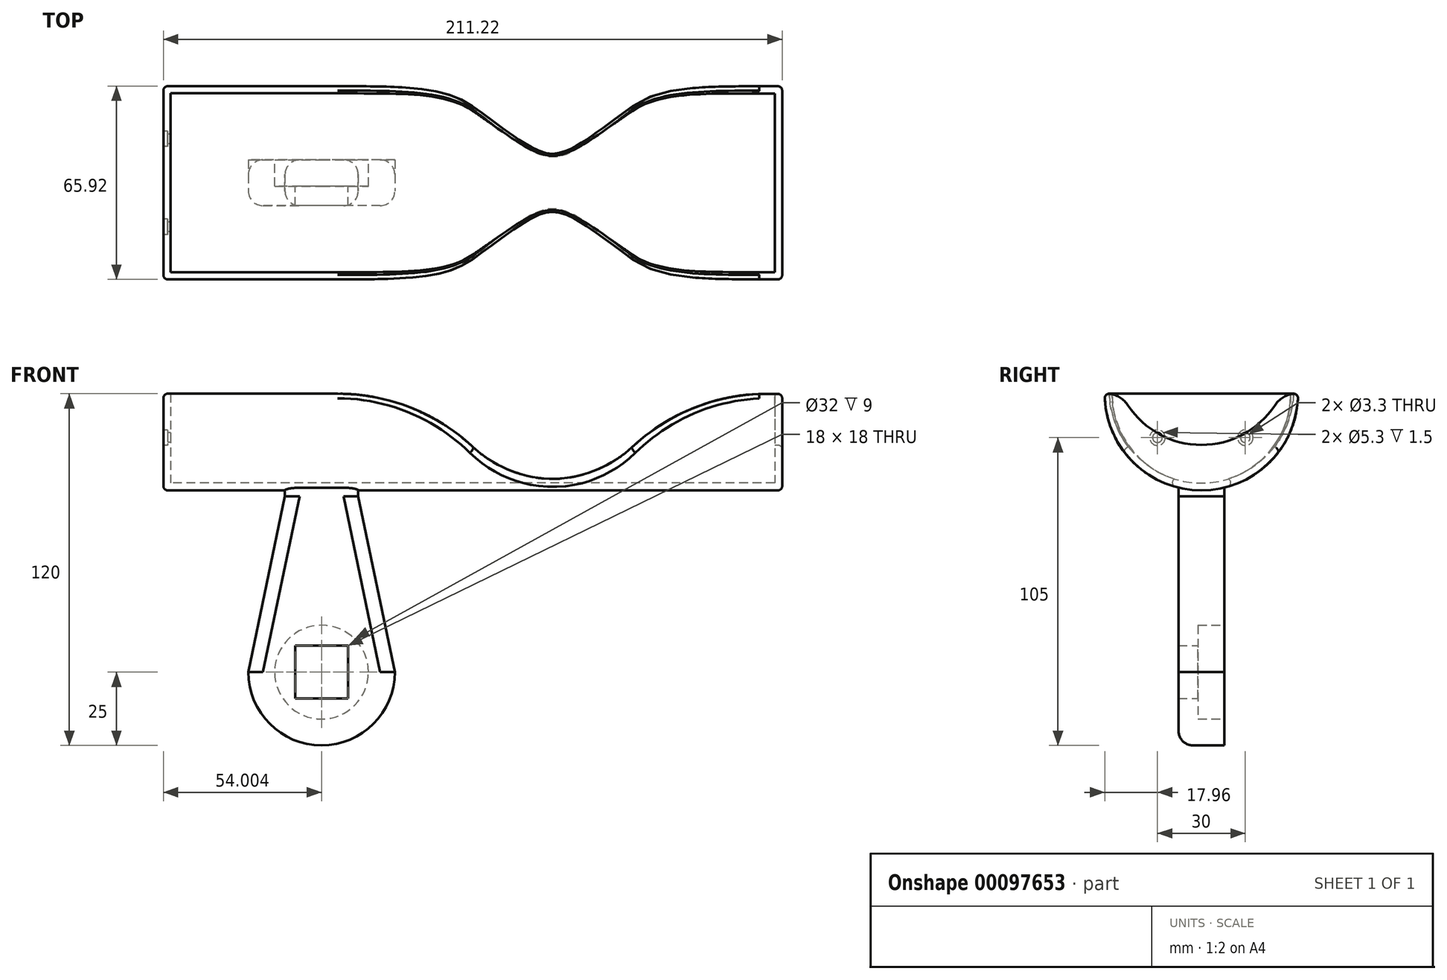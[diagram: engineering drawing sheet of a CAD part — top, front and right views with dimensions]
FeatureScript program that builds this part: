
annotation { "Feature Type Name" : "Feature", "Feature Type Description" : "" }
export const myFeature = defineFeature(function(context is Context, id is Id, definition is map)
    precondition{}
    {
        {
            var Q0;
            Q0=qCreatedBy(makeId("Right.planeOp"),FACE);
            var sketch = newSketch(context, id + "F0", { "sketchPlane" : qUnion([Q0])});
            skArc(sketch, "E0", {"start": v(-33, 0) * mm, "mid": v(0, -33) * mm, "end": v(33, 0) * mm});
            skLineSegment(sketch, "E1", {"start": v(-33, 0) * mm, "end": v(33, 0) * mm});
            skSolve(sketch);
        }
        {
            var Q0;
            Q0=makeQuery(id+"F0.imprint","IMPRINT",FACE,{"disambiguationData":[TD([[makeQuery(id+"F0.imprint","IMPRINT",EDGE,{"derivedFrom":sQuery(id+"F0.wireOp",EDGE,"E0")}),1.0]])]});
            extrude(context, id + "F1", {"entities" : qUnion([Q0]), "endBound" : BoundingType.SYMMETRIC, "depth" : 211.21 * mm});
        }
        {
            var Q0;
            Q0=makeQuery(id+"F1.opExtrude","SWEPT_FACE",FACE,{"disambiguationData":[OSD([sQuery(id+"F0.wireOp",EDGE,"E1")])]});
            shell(context, id + "F2", {"entities" : qUnion([Q0]), "thickness" : 2.5 * mm});
        }
        {
            var Q0;
            Q0=qCreatedBy(makeId("Front.planeOp"),FACE);
            var sketch = newSketch(context, id + "F3", { "sketchPlane" : qUnion([Q0])});
            skArc(sketch, "E2", {"start": v(0, -18.13) * mm, "mid": v(-21.33, -4.7) * mm, "end": v(-46.1, 0) * mm});
            skArc(sketch, "E3", {"start": v(0, -18.13) * mm, "mid": v(27.25, -28.85) * mm, "end": v(54.5, -18.13) * mm});
            skArc(sketch, "E4", {"start": v(100.6, 0) * mm, "mid": v(75.83, -4.7) * mm, "end": v(54.5, -18.13) * mm});
            skLineSegment(sketch, "E5", {"start": v(-46.1, 0) * mm, "end": v(100.6, 0) * mm});
            skSolve(sketch);
        }
        {
            var Q0;
            Q0 = qSketchRegion(id + "F3", true);
            extrude(context, id + "F4", {"entities" : qUnion([Q0]), "operationType" : NewBodyOperationType.REMOVE, "endBound" : BoundingType.SYMMETRIC, "oppositeDirection" : true, "depth" : 70 * mm});
        }
        {
            var Q0;
            Q0=makeQuery(id+"F1.opExtrude","CAP_FACE",FACE,{"disambiguationData":[OSD([sQuery(id+"F0.wireOp",EDGE,"E0"),sQuery(id+"F0.wireOp",EDGE,"E1")])],"isStart":false});
            var sketch = newSketch(context, id + "F5", { "sketchPlane" : qUnion([Q0])});
            skArc(sketch, "E6", {"start": v(-25.04, -4) * mm, "mid": v(-28.49, -0.94) * mm, "end": v(-33, 0) * mm});
            skArc(sketch, "E7", {"start": v(-25.04, -4) * mm, "mid": v(0, -17.48) * mm, "end": v(25.04, -4) * mm});
            skArc(sketch, "E8", {"start": v(33, 0) * mm, "mid": v(28.49, -0.94) * mm, "end": v(25.04, -4) * mm});
            skLineSegment(sketch, "E9", {"start": v(-33, 0) * mm, "end": v(33, 0) * mm});
            skSolve(sketch);
        }
        {
            var Q0;
            Q0=makeQuery(id+"F5.imprint","IMPRINT",FACE,{"disambiguationData":[TD([[makeQuery(id+"F5.imprint","IMPRINT",EDGE,{"derivedFrom":sQuery(id+"F5.wireOp",EDGE,"E6")}),-1.0]])]});
            extrude(context, id + "F6", {"entities" : qUnion([Q0]), "operationType" : NewBodyOperationType.REMOVE, "endBound" : BoundingType.UP_TO_NEXT, "oppositeDirection" : true, "depth" : 25 * mm});
        }
        {
            var Q0;
            Q0=makeQuery(id+"F4.boolean.opBoolean","INTERSECT",EDGE,{"disambiguationData":[OD(0.0)],"derivedFrom":[makeQuery(id+"F1.opExtrude","SWEPT_FACE",FACE,{"disambiguationData":[OSD([sQuery(id+"F0.wireOp",EDGE,"E0")])]}),makeQuery(id+"F4.opExtrude","SWEPT_FACE",FACE,{"disambiguationData":[OSD([sQuery(id+"F3.wireOp",EDGE,"E2")])]})]});
            fillet(context, id + "F7", {"entities" : qUnion([Q0]), "radius" : 1.5 * mm, "tangentPropagation" : true, "allowEdgeOverflow" : false});
        }
        {
            var Q0;
            Q0=makeQuery(id+"F4.boolean.opBoolean","INTERSECT",EDGE,{"disambiguationData":[OD(1.0)],"derivedFrom":[makeQuery(id+"F1.opExtrude","SWEPT_FACE",FACE,{"disambiguationData":[OSD([sQuery(id+"F0.wireOp",EDGE,"E0")])]}),makeQuery(id+"F4.opExtrude","SWEPT_FACE",FACE,{"disambiguationData":[OSD([sQuery(id+"F3.wireOp",EDGE,"E3")])]})]});
            fillet(context, id + "F8", {"entities" : qUnion([Q0]), "radius" : 1.5 * mm, "tangentPropagation" : true, "allowEdgeOverflow" : false});
        }
        {
            var Q0;
            Q0=makeQuery(id+"F1.opExtrude","CAP_FACE",FACE,{"disambiguationData":[OSD([sQuery(id+"F0.wireOp",EDGE,"E0"),sQuery(id+"F0.wireOp",EDGE,"E1")])],"isStart":false});
            var Q1;
            Q1=makeQuery(id+"F1.opExtrude","CAP_FACE",FACE,{"disambiguationData":[OSD([sQuery(id+"F0.wireOp",EDGE,"E0"),sQuery(id+"F0.wireOp",EDGE,"E1")])],"isStart":true});
            fillet(context, id + "F9", {"entities" : qUnion([Q0, Q1]), "radius" : 1.5 * mm, "tangentPropagation" : true, "allowEdgeOverflow" : false});
        }
        {
            var Q0;
            Q0=makeQuery(id+"F1.opExtrude","CAP_FACE",FACE,{"disambiguationData":[OSD([sQuery(id+"F0.wireOp",EDGE,"E0"),sQuery(id+"F0.wireOp",EDGE,"E1")])],"isStart":true});
            var sketch = newSketch(context, id + "F10", { "sketchPlane" : qUnion([Q0])});
            skPoint(sketch, "E10", {"position": v(15, -15) * mm});
            skPoint(sketch, "E11.MirrorP", {"position": v(-15, -15) * mm});
            skSolve(sketch);
        }
        {
            var Q0;
            Q0=sQuery(id+"F10.wireOp",VERTEX,"E10");
            var Q1;
            Q1=sQuery(id+"F10.wireOp",VERTEX,"E11.MirrorP");
            var Q2;
            Q2=makeQuery(id+"F1.opExtrude","SWEPT_BODY",BODY,{"disambiguationData":[OSD([sQuery(id+"F0.wireOp",EDGE,"E0"),sQuery(id+"F0.wireOp",EDGE,"E1")])]});
            hole(context, id + "F11", {"style" : HoleStyle.SIMPLE, "endStyle" : HoleEndStyle.BLIND, "standardTappedOrClearance" : lookupTablePath({ "standard" : "ISO", "fit" : "Normal", "size" : "M3", "type" : "Clearance" }), "standardBlindInLast" : lookupTablePath({ "fit" : "Standard", "standard" : "ISO", "size" : "M3", "type" : "Clearance" }), "holeDiameter" : 3.3 * mm, "holeDepth" : 2.5 * mm, "locations" : qUnion([Q0, Q1]), "scope" : qUnion([Q2])});
        }
        {
            var Q0;
            Q0=makeQuery(id+"F1.opExtrude","CAP_FACE",FACE,{"disambiguationData":[OSD([sQuery(id+"F0.wireOp",EDGE,"E0"),sQuery(id+"F0.wireOp",EDGE,"E1")])],"isStart":true});
            var sketch = newSketch(context, id + "F12", { "sketchPlane" : qUnion([Q0])});
            skCircle(sketch, "E12", {"center": v(15, -15) * mm, "radius": 2.65 * mm});
            skCircle(sketch, "E13.MirrorC", {"center": v(-15, -15) * mm, "radius": 2.65 * mm});
            skSolve(sketch);
        }
        {
            var Q0;
            Q0 = qSketchRegion(id + "F12", true);
            extrude(context, id + "F13", {"entities" : qUnion([Q0]), "operationType" : NewBodyOperationType.REMOVE, "oppositeDirection" : true, "depth" : 1.5 * mm});
        }
        {
            var Q0;
            Q0=qCreatedBy(makeId("Top.planeOp"),FACE);
            cPlane(context, id + "F14", {"entities" : qUnion([Q0]), "cplaneType" : CPlaneType.OFFSET, "offset" : 35 * mm, "oppositeDirection" : true, "width" : 150 * mm, "height" : 150 * mm});
        }
        {
            var Q0;
            Q0=qCreatedBy(id+"F14.planeOp",FACE);
            var sketch = newSketch(context, id + "F15", { "sketchPlane" : qUnion([Q0])});
            skLineSegment(sketch, "E14.bottom", {"start": v(-59.1, -7.83) * mm, "end": v(-44.1, -7.83) * mm});
            skLineSegment(sketch, "E14.top", {"start": v(-59.1, 7.83) * mm, "end": v(-44.1, 7.83) * mm});
            skLineSegment(sketch, "E14.left", {"start": v(-64.1, -2.82) * mm, "end": v(-64.1, 2.82) * mm});
            skLineSegment(sketch, "E14.right", {"start": v(-39.1, -2.83) * mm, "end": v(-39.1, 2.83) * mm});
            skPoint(sketch, "E15.visualSharp", {"position": v(-64.1, -7.82) * mm});
            skArc(sketch, "E15.filletArc", {"start": v(-64.1, -2.82) * mm, "mid": v(-62.64, -6.36) * mm, "end": v(-59.1, -7.82) * mm});
            skPoint(sketch, "E16.visualSharp", {"position": v(-64.1, 7.82) * mm});
            skArc(sketch, "E16.filletArc", {"start": v(-59.1, 7.82) * mm, "mid": v(-62.64, 6.36) * mm, "end": v(-64.1, 2.82) * mm});
            skPoint(sketch, "E17.visualSharp", {"position": v(-39.1, -7.83) * mm});
            skArc(sketch, "E17.filletArc", {"start": v(-44.1, -7.83) * mm, "mid": v(-40.57, -6.36) * mm, "end": v(-39.1, -2.83) * mm});
            skPoint(sketch, "E18.visualSharp", {"position": v(-39.1, 7.83) * mm});
            skArc(sketch, "E18.filletArc", {"start": v(-39.1, 2.83) * mm, "mid": v(-40.57, 6.36) * mm, "end": v(-44.1, 7.83) * mm});
            skSolve(sketch);
        }
        {
            var Q0;
            Q0=qCreatedBy(id+"F14.planeOp",FACE);
            cPlane(context, id + "F16", {"entities" : qUnion([Q0]), "cplaneType" : CPlaneType.OFFSET, "offset" : 60 * mm, "oppositeDirection" : true, "width" : 150 * mm, "height" : 150 * mm});
        }
        {
            var Q0;
            Q0=qCreatedBy(id+"F16.planeOp",FACE);
            var sketch = newSketch(context, id + "F17", { "sketchPlane" : qUnion([Q0])});
            skLineSegment(sketch, "E19.bottom", {"start": v(-71.6, 7.83) * mm, "end": v(-31.6, 7.83) * mm});
            skLineSegment(sketch, "E19.top", {"start": v(-71.6, -7.83) * mm, "end": v(-31.6, -7.83) * mm});
            skLineSegment(sketch, "E19.left", {"start": v(-76.6, 2.82) * mm, "end": v(-76.6, -2.83) * mm});
            skLineSegment(sketch, "E19.right", {"start": v(-26.6, 2.83) * mm, "end": v(-26.6, -2.82) * mm});
            skPoint(sketch, "E20.visualSharp", {"position": v(-76.6, 7.83) * mm});
            skArc(sketch, "E20.filletArc", {"start": v(-71.6, 7.83) * mm, "mid": v(-75.14, 6.36) * mm, "end": v(-76.6, 2.82) * mm});
            skPoint(sketch, "E21.visualSharp", {"position": v(-26.6, 7.83) * mm});
            skArc(sketch, "E21.filletArc", {"start": v(-26.6, 2.83) * mm, "mid": v(-28.07, 6.36) * mm, "end": v(-31.6, 7.83) * mm});
            skPoint(sketch, "E22.visualSharp", {"position": v(-26.6, -7.83) * mm});
            skArc(sketch, "E22.filletArc", {"start": v(-31.6, -7.83) * mm, "mid": v(-28.07, -6.36) * mm, "end": v(-26.6, -2.82) * mm});
            skPoint(sketch, "E23.visualSharp", {"position": v(-76.6, -7.83) * mm});
            skArc(sketch, "E23.filletArc", {"start": v(-76.6, -2.83) * mm, "mid": v(-75.14, -6.36) * mm, "end": v(-71.6, -7.83) * mm});
            skSolve(sketch);
        }
        {
            var Q0;
            Q0=makeQuery(id+"F15.imprint","IMPRINT",FACE,{"disambiguationData":[TD([[makeQuery(id+"F15.imprint","IMPRINT",EDGE,{"derivedFrom":sQuery(id+"F15.wireOp",EDGE,"E14.bottom")}),1.0]])]});
            var Q1;
            Q1=makeQuery(id+"F1.opExtrude","SWEPT_FACE",FACE,{"disambiguationData":[OSD([sQuery(id+"F0.wireOp",EDGE,"E0")])]});
            var Q2;
            Q2=makeQuery(id+"F1.opExtrude","SWEPT_BODY",BODY,{"disambiguationData":[OSD([sQuery(id+"F0.wireOp",EDGE,"E0"),sQuery(id+"F0.wireOp",EDGE,"E1")])]});
            extrude(context, id + "F18", {"entities" : qUnion([Q0]), "operationType" : NewBodyOperationType.ADD, "endBound" : BoundingType.UP_TO_NEXT, "endBoundEntityFace" : qUnion([Q1]), "endBoundEntityBody" : qUnion([Q2]), "depth" : 25 * mm});
        }
        {
            var Q1;
            Q1=makeQuery(id+"F17.imprint","IMPRINT",FACE,{"disambiguationData":[TD([[makeQuery(id+"F17.imprint","IMPRINT",EDGE,{"derivedFrom":sQuery(id+"F17.wireOp",EDGE,"E19.bottom")}),-1.0]])]});
            var Q2;
            Q2=makeQuery(id+"F15.imprint","IMPRINT",FACE,{"disambiguationData":[TD([[makeQuery(id+"F15.imprint","IMPRINT",EDGE,{"derivedFrom":sQuery(id+"F15.wireOp",EDGE,"E14.bottom")}),1.0]])]});
            loft(context, id + "F19", {"operationType" : NewBodyOperationType.ADD, "sheetProfilesArray" : [{ "sheetProfileEntities" : qUnion([Q1]) }, { "sheetProfileEntities" : qUnion([Q2]) }]});
        }
        {
            var Q0;
            Q0=makeQuery(id+"F19.opLoft","SWEPT_FACE",FACE,{"disambiguationData":[OSD([sQuery(id+"F15.wireOp",EDGE,"E14.bottom"),sQuery(id+"F15.wireOp",EDGE,"E15.filletArc"),sQuery(id+"F15.wireOp",EDGE,"E17.filletArc"),sQuery(id+"F17.wireOp",EDGE,"E19.top"),sQuery(id+"F17.wireOp",EDGE,"E22.filletArc"),sQuery(id+"F17.wireOp",EDGE,"E23.filletArc")])]});
            var sketch = newSketch(context, id + "F20", { "sketchPlane" : qUnion([Q0])});
            skArc(sketch, "E24", {"start": v(-76.6, -95) * mm, "mid": v(-51.6, -120) * mm, "end": v(-26.6, -95) * mm});
            skLineSegment(sketch, "E25", {"start": v(-26.6, -95) * mm, "end": v(-76.6, -95) * mm});
            skSolve(sketch);
        }
        {
            var Q0;
            {var subQ0=sQuery(id+"F20.wireOp",EDGE,"E24");Q0=makeQuery(id+"F20.imprint","IMPRINT",FACE,{"disambiguationData":[TD([[makeQuery(id+"F20.imprint","IMPRINT",EDGE,{"derivedFrom":subQ0}),1.0]])]});}
            var Q1;
            Q1=makeQuery(id+"F19.opLoft","SWEPT_FACE",FACE,{"disambiguationData":[OSD([sQuery(id+"F15.wireOp",EDGE,"E14.top"),sQuery(id+"F15.wireOp",EDGE,"E16.filletArc"),sQuery(id+"F15.wireOp",EDGE,"E18.filletArc"),sQuery(id+"F17.wireOp",EDGE,"E19.bottom"),sQuery(id+"F17.wireOp",EDGE,"E20.filletArc"),sQuery(id+"F17.wireOp",EDGE,"E21.filletArc")])]});
            extrude(context, id + "F21", {"entities" : qUnion([Q0]), "operationType" : NewBodyOperationType.ADD, "endBound" : BoundingType.UP_TO_SURFACE, "oppositeDirection" : true, "endBoundEntityFace" : qUnion([Q1]), "depth" : 25 * mm});
        }
        {
            var Q0;
            Q0=makeQuery(id+"F21.opExtrude","CAP_EDGE",EDGE,{"disambiguationData":[OSD([sQuery(id+"F20.wireOp",EDGE,"E24")])],"isStart":true});
            var Q1;
            Q1=makeQuery(id+"F21.opExtrude","TWEAK_EDGE",EDGE,{"derivedFrom":[makeQuery(id+"F19.opLoft","SWEPT_FACE",FACE,{"disambiguationData":[OSD([sQuery(id+"F15.wireOp",EDGE,"E14.top"),sQuery(id+"F15.wireOp",EDGE,"E16.filletArc"),sQuery(id+"F15.wireOp",EDGE,"E18.filletArc"),sQuery(id+"F17.wireOp",EDGE,"E19.bottom"),sQuery(id+"F17.wireOp",EDGE,"E20.filletArc"),sQuery(id+"F17.wireOp",EDGE,"E21.filletArc")])]}),makeQuery(id+"F20.imprint","IMPRINT",EDGE,{"derivedFrom":sQuery(id+"F20.wireOp",EDGE,"E24")})]});
            fillet(context, id + "F22", {"entities" : qUnion([Q0, Q1]), "radius" : 5 * mm, "tangentPropagation" : true, "allowEdgeOverflow" : false});
        }
        {
            var Q0;
            Q0=makeQuery(id+"F15.imprint","IMPRINT",FACE,{"disambiguationData":[TD([[makeQuery(id+"F15.imprint","IMPRINT",EDGE,{"derivedFrom":sQuery(id+"F15.wireOp",EDGE,"E14.bottom")}),1.0]])]});
            var Q1;
            Q1=makeQuery(id+"F2.opShell","OFFSET_FACE",FACE,{"disambiguationData":[OSD([sQuery(id+"F0.wireOp",EDGE,"E0")])]});
            extrude(context, id + "F23", {"entities" : qUnion([Q0]), "endBound" : BoundingType.UP_TO_SURFACE, "endBoundEntityFace" : qUnion([Q1]), "depth" : 25 * mm});
        }
        {
            var Q0;
            Q0=makeQuery(id+"F23.opExtrude","SWEPT_BODY",BODY,{"disambiguationData":[OSD([sQuery(id+"F15.wireOp",EDGE,"E14.bottom"),sQuery(id+"F15.wireOp",EDGE,"E14.top"),sQuery(id+"F15.wireOp",EDGE,"E14.left"),sQuery(id+"F15.wireOp",EDGE,"E14.right"),sQuery(id+"F15.wireOp",EDGE,"E15.filletArc"),sQuery(id+"F15.wireOp",EDGE,"E16.filletArc"),sQuery(id+"F15.wireOp",EDGE,"E17.filletArc"),sQuery(id+"F15.wireOp",EDGE,"E18.filletArc")])]});
            deleteBodies(context, id + "F24", {"entities" : qUnion([Q0])});
        }
        {
            var Q0;
            {var subQ0=sQuery(id+"F17.wireOp",EDGE,"E21.filletArc");var subQ1=sQuery(id+"F17.wireOp",EDGE,"E20.filletArc");var subQ2=sQuery(id+"F17.wireOp",EDGE,"E19.bottom");var subQ3=sQuery(id+"F15.wireOp",EDGE,"E18.filletArc");var subQ4=sQuery(id+"F15.wireOp",EDGE,"E16.filletArc");var subQ5=sQuery(id+"F15.wireOp",EDGE,"E14.top");Q0=makeQuery(id+"F21.boolean.opBoolean","MERGE",FACE,{"derivedFrom":[makeQuery(id+"F19.boolean.opBoolean","MERGE",FACE,{"derivedFrom":[makeQuery(id+"F18.opExtrude","SWEPT_FACE",FACE,{"disambiguationData":[OSD([subQ5])]}),makeQuery(id+"F19.opLoft","SWEPT_FACE",FACE,{"disambiguationData":[OSD([subQ5,subQ4,subQ3,subQ2,subQ1,subQ0])]})]}),makeQuery(id+"F21.opExtrude","CAP_FACE",FACE,{"disambiguationData":[OSD([subQ5,subQ4,subQ3,subQ2,subQ1,subQ0])],"isStart":false})]});}
            var sketch = newSketch(context, id + "F25", { "sketchPlane" : qUnion([Q0])});
            skCircle(sketch, "E26", {"center": v(51.6, -95) * mm, "radius": 16 * mm});
            skLineSegment(sketch, "E27.bottom", {"start": v(42.6, -104) * mm, "end": v(60.6, -104) * mm});
            skLineSegment(sketch, "E27.top", {"start": v(42.6, -86) * mm, "end": v(60.6, -86) * mm});
            skLineSegment(sketch, "E27.left", {"start": v(42.6, -104) * mm, "end": v(42.6, -86) * mm});
            skLineSegment(sketch, "E27.right", {"start": v(60.6, -104) * mm, "end": v(60.6, -86) * mm});
            skSolve(sketch);
        }
        {
            var Q0;
            Q0=makeQuery(id+"F25.imprint","IMPRINT",FACE,{"disambiguationData":[TD([[makeQuery(id+"F25.imprint","IMPRINT",EDGE,{"derivedFrom":sQuery(id+"F25.wireOp",EDGE,"E26")}),1.0]])]});
            extrude(context, id + "F26", {"entities" : qUnion([Q0]), "operationType" : NewBodyOperationType.REMOVE, "oppositeDirection" : true, "depth" : 9 * mm});
        }
        {
            var Q0;
            {var subQ0=sQuery(id+"F17.wireOp",EDGE,"E21.filletArc");var subQ1=sQuery(id+"F17.wireOp",EDGE,"E20.filletArc");var subQ2=sQuery(id+"F17.wireOp",EDGE,"E19.bottom");var subQ3=sQuery(id+"F15.wireOp",EDGE,"E18.filletArc");var subQ4=sQuery(id+"F15.wireOp",EDGE,"E16.filletArc");var subQ5=sQuery(id+"F15.wireOp",EDGE,"E14.top");Q0=makeQuery(id+"F26.boolean.opBoolean","SPLIT",FACE,{"disambiguationData":[TD([makeQuery(id+"F26.opExtrude","SWEPT_FACE",FACE,{"disambiguationData":[OSD([sQuery(id+"F25.wireOp",EDGE,"E27.bottom")])]})])],"derivedFrom":makeQuery(id+"F21.boolean.opBoolean","MERGE",FACE,{"derivedFrom":[makeQuery(id+"F19.boolean.opBoolean","MERGE",FACE,{"derivedFrom":[makeQuery(id+"F18.opExtrude","SWEPT_FACE",FACE,{"disambiguationData":[OSD([subQ5])]}),makeQuery(id+"F19.opLoft","SWEPT_FACE",FACE,{"disambiguationData":[OSD([subQ5,subQ4,subQ3,subQ2,subQ1,subQ0])]})]}),makeQuery(id+"F21.opExtrude","CAP_FACE",FACE,{"disambiguationData":[OSD([subQ5,subQ4,subQ3,subQ2,subQ1,subQ0])],"isStart":false})]})});}
            extrude(context, id + "F27", {"entities" : qUnion([Q0]), "operationType" : NewBodyOperationType.REMOVE, "oppositeDirection" : true, "depth" : 19 * mm});
        }
    });
